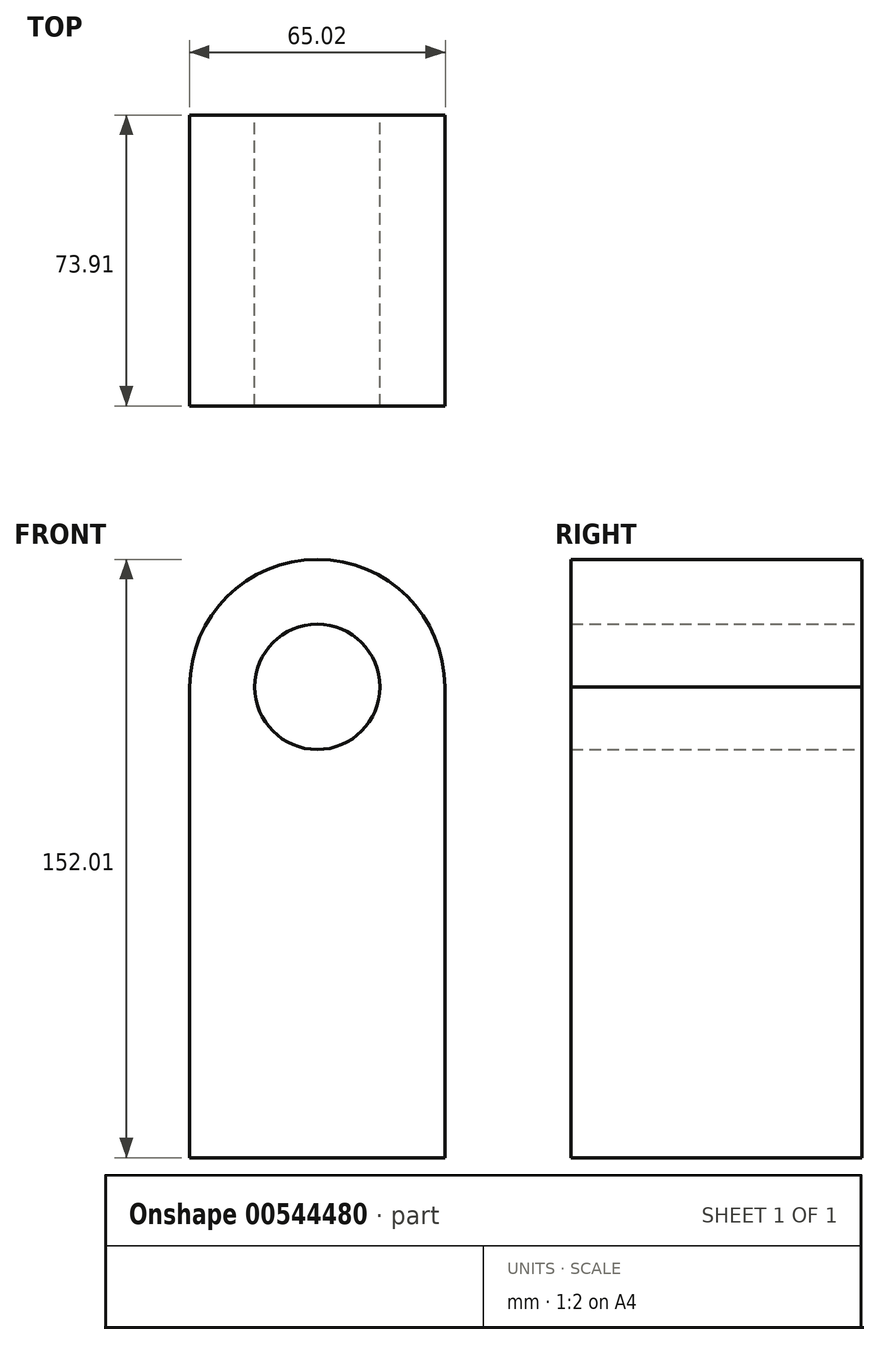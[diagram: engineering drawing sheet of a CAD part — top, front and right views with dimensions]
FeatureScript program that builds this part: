
annotation { "Feature Type Name" : "Feature", "Feature Type Description" : "" }
export const myFeature = defineFeature(function(context is Context, id is Id, definition is map)
    precondition{}
    {
        {
            var Q0;
            Q0=qCreatedBy(makeId("Front.planeOp"),FACE);
            var sketch = newSketch(context, id + "F0", { "sketchPlane" : qUnion([Q0])});
            skLineSegment(sketch, "E0.bottom", {"start": v(32.5, -59.81) * mm, "end": v(-32.5, -59.81) * mm});
            skLineSegment(sketch, "E0.top", {"start": v(32.5, 59.81) * mm, "end": v(32.39, 59.81) * mm});
            skLineSegment(sketch, "E0.left", {"start": v(32.5, -59.81) * mm, "end": v(32.5, 59.81) * mm});
            skLineSegment(sketch, "E0.right", {"start": v(-32.5, -59.81) * mm, "end": v(-32.5, 59.81) * mm});
            skPoint(sketch, "E0.middle", {"position": v(0, 0) * mm});
            skCircle(sketch, "E1", {"center": v(0, 59.81) * mm, "radius": 15.93 * mm});
            skArc(sketch, "E2", {"start": v(-32.39, 59.81) * mm, "mid": v(0, 92.2) * mm, "end": v(32.39, 59.81) * mm});
            skLineSegment(sketch, "E3.trimOffspring", {"start": v(-32.39, 59.81) * mm, "end": v(-32.5, 59.81) * mm});
            skSolve(sketch);
        }
        {
            var Q0;
            Q0=makeQuery(id+"F0.imprint","IMPRINT",FACE,{"disambiguationData":[TD([[makeQuery(id+"F0.imprint","IMPRINT",EDGE,{"derivedFrom":sQuery(id+"F0.wireOp",EDGE,"E0.bottom")}),-1.0]])]});
            extrude(context, id + "F1", {"entities" : qUnion([Q0]), "depth" : 73.9 * mm, "offsetDistance" : 25.4 * mm});
        }
    });
